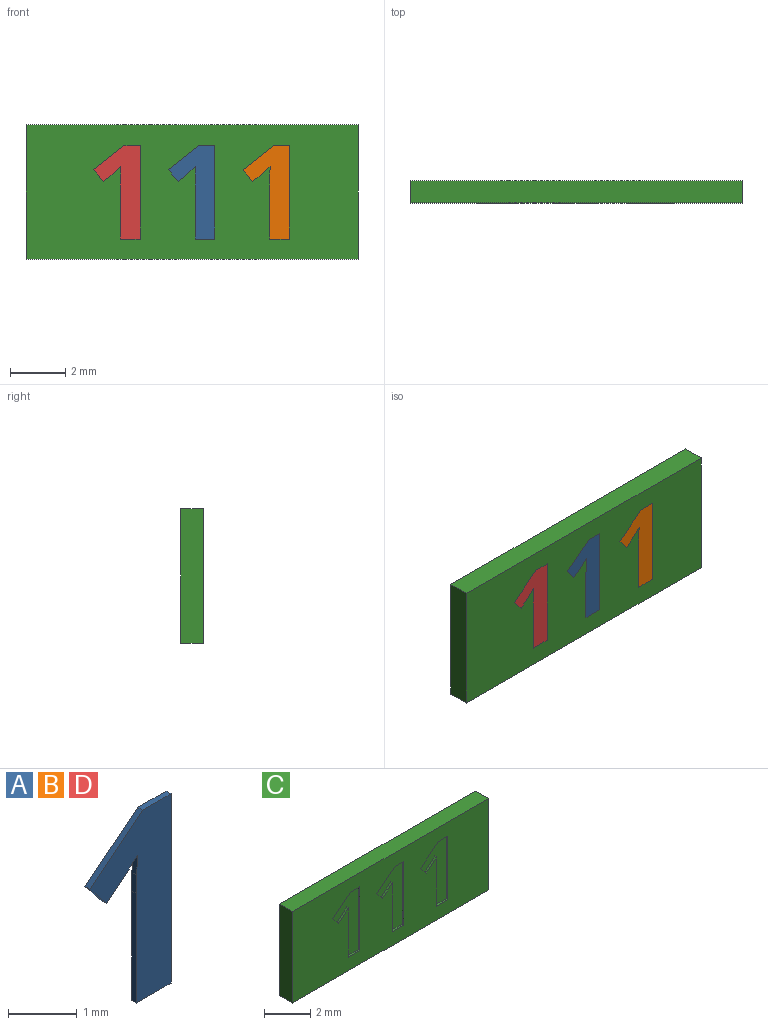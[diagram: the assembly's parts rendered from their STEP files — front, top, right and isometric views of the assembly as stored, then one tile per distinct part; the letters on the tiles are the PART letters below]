
ASSEMBLY  parts=4 mates=3
PART A: 12 faces, bbox 1.7x0.1x3.4 mm
  f0: plane 3.37x1.67mm, normal (0,-1,0), area 2.9mm2, adj f1,f2,f3,f4,f5,f6,f7,f9
  f1: plane 0.59x0.1mm, normal (0,0,1), area 0.1mm2, adj f0,f2,f8,f10
  f2: plane 1.09x0.86mm, normal (-0.62,0,0.78), area 0.1mm2, adj f0,f1,f3,f8
  f3: plane 0.43x0.34mm, normal (-0.78,0,-0.63), area 0.1mm2, adj f0,f2,f4,f8
  f4: plane 0.39x0.31mm, normal (0.63,0,-0.78), area 0mm2, adj f0,f3,f5,f8
  f5: extruded ~0.25x0.23mm, area 0mm2, adj f0,f4,f6,f8
  f6: plane 0.35x0.1mm, normal (-1,0,0.03), area 0mm2, adj f0,f5,f7,f8
  f7: plane 0.32x0.1mm, normal (-1,0,0.02), area 0mm2, adj f0,f6,f8,f9
  f8: plane 3.37x1.67mm, normal (0,1,0), area 2.9mm2, adj f1,f2,f3,f4,f5,f6,f7,f9
  f9: plane 1.95x0.1mm, normal (-1,0,0), area 0.2mm2, adj f0,f7,f8,f11
  f10: plane 3.37x0.1mm, normal (1,0,0), area 0.3mm2, adj f0,f1,f8,f11
  f11: plane 0.71x0.1mm, normal (0,0,-1), area 0.1mm2, adj f0,f8,f9,f10
PART B: same geometry as A
PART C: 39 faces, bbox 12x0.8x4.9 mm
  f0: plane 12x4.85mm, normal (0,-1,0), area 49.4mm2, adj f1,f2,f3,f4,f6,f7,f8,f9
  f1: plane 4.85x0.8mm, normal (1,0,0), area 3.9mm2, adj f0,f2,f4,f5
  f2: plane 12x0.8mm, normal (0,0,1), area 9.6mm2, adj f0,f1,f3,f5
  f3: plane 4.85x0.8mm, normal (-1,0,0), area 3.9mm2, adj f0,f2,f4,f5
  f4: plane 12x0.8mm, normal (0,0,-1), area 9.6mm2, adj f0,f1,f3,f5
  f5: plane 12x4.85mm, normal (0,1,0), area 58.2mm2, adj f1,f2,f3,f4
  f6: plane 3.37x0.1mm, normal (-1,0,0), area 0.3mm2, adj f0,f7,f15,f16
  f7: plane 0.59x0.1mm, normal (0,0,-1), area 0.1mm2, adj f0,f6,f8,f16
  f8: plane 1.09x0.86mm, normal (0.62,0,-0.78), area 0.1mm2, adj f0,f7,f9,f16
  f9: plane 0.43x0.34mm, normal (0.78,0,0.63), area 0.1mm2, adj f0,f8,f10,f16
  f10: plane 0.39x0.31mm, normal (-0.63,0,0.78), area 0mm2, adj f0,f9,f11,f16
  f11: extruded ~0.25x0.23mm, area 0mm2, adj f0,f10,f12,f16
  f12: plane 0.35x0.1mm, normal (1,0,-0.03), area 0mm2, adj f0,f11,f13,f16
  f13: plane 0.32x0.1mm, normal (1,0,-0.02), area 0mm2, adj f0,f12,f14,f16
  f14: plane 1.95x0.1mm, normal (1,0,0), area 0.2mm2, adj f0,f13,f15,f16
  f15: plane 0.71x0.1mm, normal (0,0,1), area 0.1mm2, adj f0,f6,f14,f16
  f16: plane 3.37x1.67mm, normal (0,-1,0), area 2.9mm2, adj f6,f7,f8,f9,f10,f11,f12,f13
  f17: plane 3.37x0.1mm, normal (-1,0,0), area 0.3mm2, adj f0,f18,f26,f27
  f18: plane 0.59x0.1mm, normal (0,0,-1), area 0.1mm2, adj f0,f17,f19,f27
  f19: plane 1.09x0.86mm, normal (0.62,0,-0.78), area 0.1mm2, adj f0,f18,f20,f27
  f20: plane 0.43x0.34mm, normal (0.78,0,0.63), area 0.1mm2, adj f0,f19,f21,f27
  f21: plane 0.39x0.31mm, normal (-0.63,0,0.78), area 0mm2, adj f0,f20,f22,f27
  f22: extruded ~0.25x0.23mm, area 0mm2, adj f0,f21,f23,f27
  f23: plane 0.35x0.1mm, normal (1,0,-0.03), area 0mm2, adj f0,f22,f24,f27
  f24: plane 0.32x0.1mm, normal (1,0,-0.02), area 0mm2, adj f0,f23,f25,f27
  f25: plane 1.95x0.1mm, normal (1,0,0), area 0.2mm2, adj f0,f24,f26,f27
  f26: plane 0.71x0.1mm, normal (0,0,1), area 0.1mm2, adj f0,f17,f25,f27
  f27: plane 3.37x1.67mm, normal (0,-1,0), area 2.9mm2, adj f17,f18,f19,f20,f21,f22,f23,f24
  f28: plane 3.37x0.1mm, normal (-1,0,0), area 0.3mm2, adj f0,f29,f37,f38
  f29: plane 0.59x0.1mm, normal (0,0,-1), area 0.1mm2, adj f0,f28,f30,f38
  f30: plane 1.09x0.86mm, normal (0.62,0,-0.78), area 0.1mm2, adj f0,f29,f31,f38
  f31: plane 0.43x0.34mm, normal (0.78,0,0.63), area 0.1mm2, adj f0,f30,f32,f38
  f32: plane 0.39x0.31mm, normal (-0.63,0,0.78), area 0mm2, adj f0,f31,f33,f38
  f33: extruded ~0.25x0.23mm, area 0mm2, adj f0,f32,f34,f38
  f34: plane 0.35x0.1mm, normal (1,0,-0.03), area 0mm2, adj f0,f33,f35,f38
  f35: plane 0.32x0.1mm, normal (1,0,-0.02), area 0mm2, adj f0,f34,f36,f38
  f36: plane 1.95x0.1mm, normal (1,0,0), area 0.2mm2, adj f0,f35,f37,f38
  f37: plane 0.71x0.1mm, normal (0,0,1), area 0.1mm2, adj f0,f28,f36,f38
  f38: plane 3.37x1.67mm, normal (0,-1,0), area 2.9mm2, adj f28,f29,f30,f31,f32,f33,f34,f35
PART D: same geometry as A
PLACE A t=(-1.61,0.38,0.01)mm
PLACE B t=(1.09,0.38,0.01)mm
PLACE C t=(-0.04,0.38,0.01)mm
PLACE D t=(-4.31,0.38,0.01)mm
MATE fastened A.f0 <-> C.f0  axis (0,-1,0) through (0.07,-0.42,-1.69)mm
MATE fastened B.f0 <-> C.f0  axis (0,-1,0) through (2.76,-0.42,-1.69)mm
MATE fastened D.f0 <-> C.f0  axis (0,-1,0) through (-2.63,-0.42,-1.69)mm
